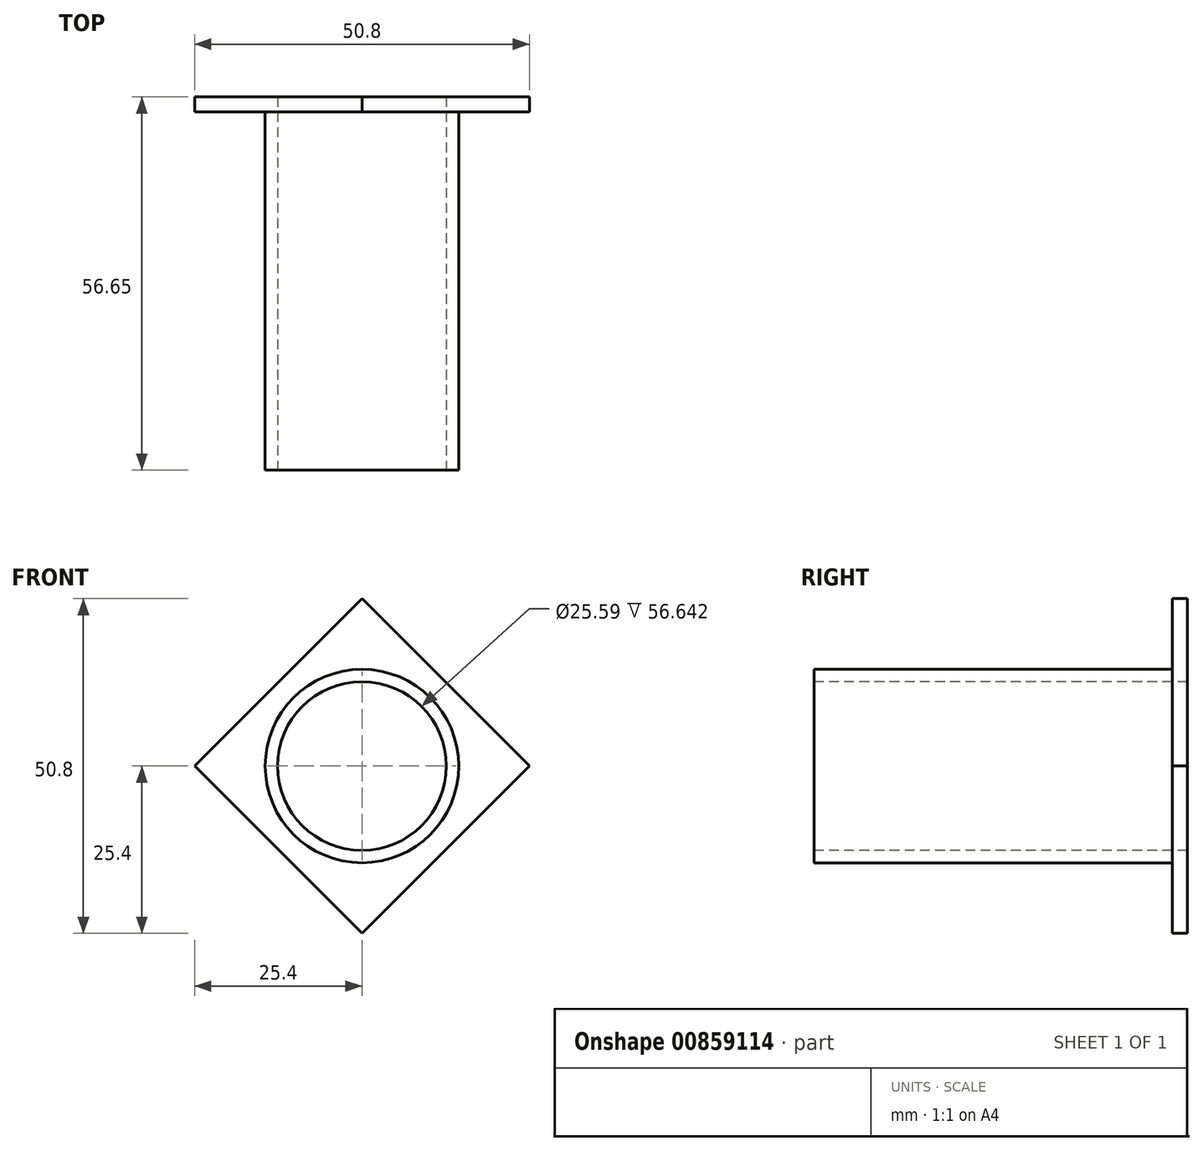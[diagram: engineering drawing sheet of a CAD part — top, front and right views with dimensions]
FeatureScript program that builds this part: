
annotation { "Feature Type Name" : "Feature", "Feature Type Description" : "" }
export const myFeature = defineFeature(function(context is Context, id is Id, definition is map)
    precondition{}
    {
        {
            var Q0;
            Q0=qCreatedBy(makeId("Front.planeOp"),FACE);
            var sketch = newSketch(context, id + "F0", { "sketchPlane" : qUnion([Q0])});
            skLineSegment(sketch, "E0", {"start": v(-25.4, 0) * mm, "end": v(0, 25.4) * mm});
            skLineSegment(sketch, "E1", {"start": v(0, 25.4) * mm, "end": v(25.4, 0) * mm});
            skLineSegment(sketch, "E2", {"start": v(25.4, 0) * mm, "end": v(0, -25.4) * mm});
            skLineSegment(sketch, "E3", {"start": v(0, -25.4) * mm, "end": v(-25.4, 0) * mm});
            skSolve(sketch);
        }
        {
            var Q0;
            Q0=qCreatedBy(makeId("Front.planeOp"),FACE);
            var sketch = newSketch(context, id + "F1", { "sketchPlane" : qUnion([Q0])});
            skCircle(sketch, "E4", {"center": v(0, 0) * mm, "radius": 14.68 * mm});
            skSolve(sketch);
        }
        {
            var Q0;
            Q0=makeQuery(id+"F0.imprint","IMPRINT",FACE,{"disambiguationData":[TD([[makeQuery(id+"F0.imprint","IMPRINT",EDGE,{"derivedFrom":sQuery(id+"F0.wireOp",EDGE,"E0")}),-1.0]])]});
            extrude(context, id + "F2", {"entities" : qUnion([Q0]), "oppositeDirection" : true, "depth" : 2.3 * mm, "offsetDistance" : 25.4 * mm});
        }
        {
            var Q0;
            Q0 = qSketchRegion(id + "F1", true);
            extrude(context, id + "F3", {"entities" : qUnion([Q0]), "operationType" : NewBodyOperationType.ADD, "depth" : 54.36 * mm, "offsetDistance" : 25.4 * mm});
        }
        {
            var Q0;
            Q0=makeQuery(id+"F3.opExtrude","CAP_FACE",FACE,{"disambiguationData":[OSD([sQuery(id+"F1.wireOp",EDGE,"E4")])],"isStart":false});
            var sketch = newSketch(context, id + "F4", { "sketchPlane" : qUnion([Q0])});
            skCircle(sketch, "E5", {"center": v(0, 0) * mm, "radius": 12.8 * mm});
            skSolve(sketch);
        }
        {
            var Q0;
            Q0 = qSketchRegion(id + "F4", true);
            extrude(context, id + "F5", {"entities" : qUnion([Q0]), "operationType" : NewBodyOperationType.REMOVE, "oppositeDirection" : true, "depth" : 76.2 * mm, "offsetDistance" : 25.4 * mm});
        }
    });
